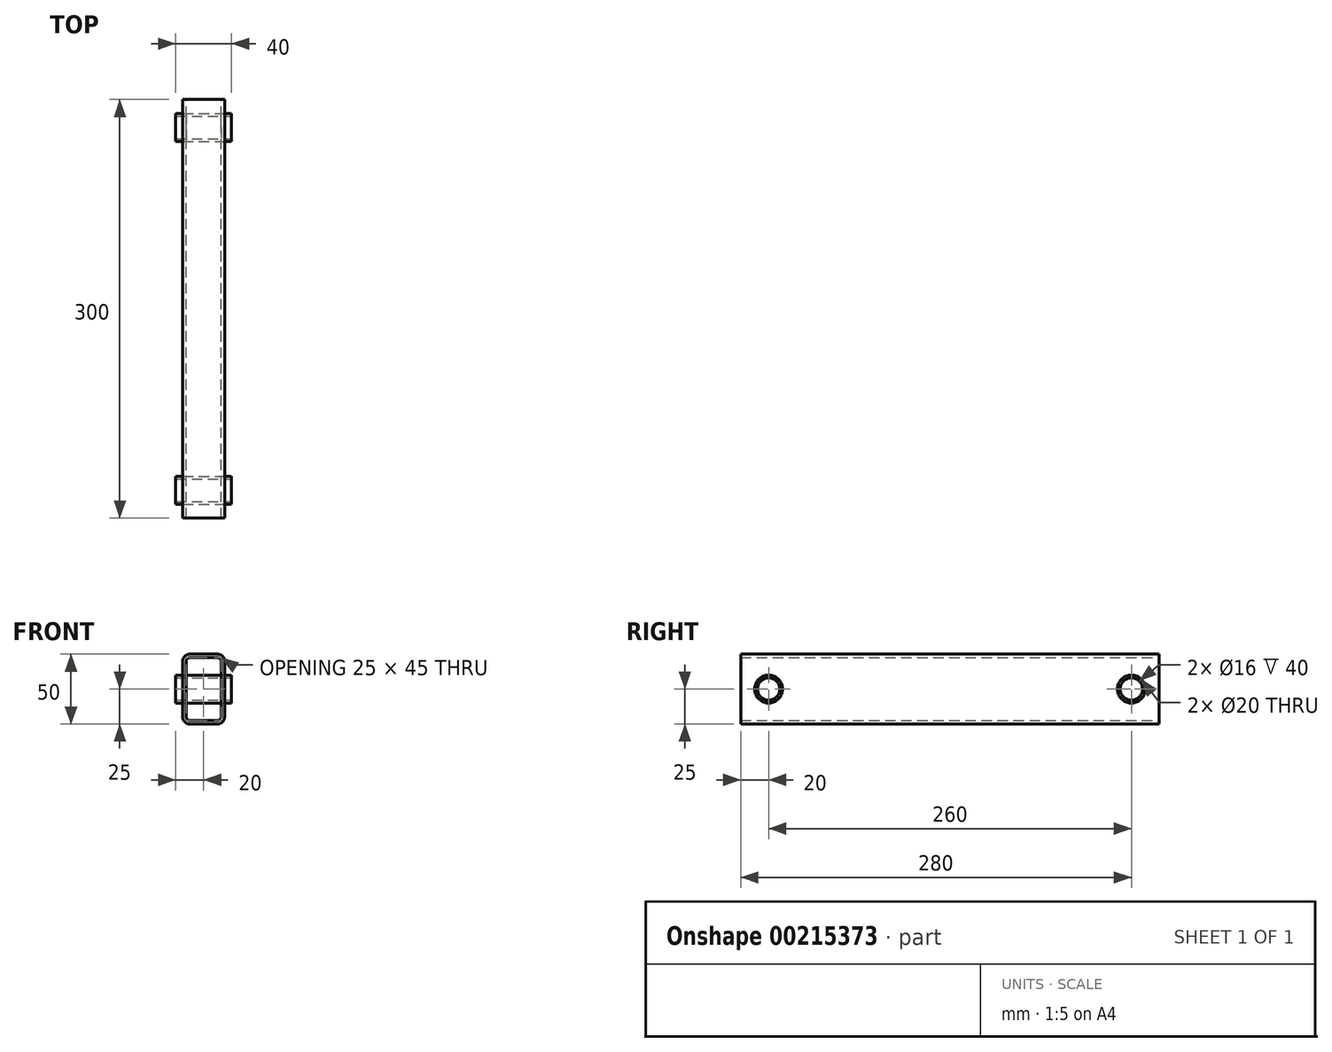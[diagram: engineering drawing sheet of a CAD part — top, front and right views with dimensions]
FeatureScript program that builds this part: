
annotation { "Feature Type Name" : "Feature", "Feature Type Description" : "" }
export const myFeature = defineFeature(function(context is Context, id is Id, definition is map)
    precondition{}
    {
        {
            var Q0;
            Q0=qCreatedBy(makeId("Front.planeOp"),FACE);
            var sketch = newSketch(context, id + "F0", { "sketchPlane" : qUnion([Q0])});
            skLineSegment(sketch, "E0.bottom", {"start": v(10, -25) * mm, "end": v(-10, -25) * mm});
            skLineSegment(sketch, "E0.top", {"start": v(10, 25) * mm, "end": v(-10, 25) * mm});
            skLineSegment(sketch, "E0.left", {"start": v(15, -20) * mm, "end": v(15, 20) * mm});
            skLineSegment(sketch, "E0.right", {"start": v(-15, -20) * mm, "end": v(-15, 20) * mm});
            skPoint(sketch, "E0.middle", {"position": v(0, 0) * mm});
            skPoint(sketch, "E1.visualSharp", {"position": v(-15, 25) * mm});
            skArc(sketch, "E1.filletArc", {"start": v(-10, 25) * mm, "mid": v(-13.54, 23.54) * mm, "end": v(-15, 20) * mm});
            skPoint(sketch, "E2.visualSharp", {"position": v(-15, -25) * mm});
            skArc(sketch, "E2.filletArc", {"start": v(-15, -20) * mm, "mid": v(-13.54, -23.54) * mm, "end": v(-10, -25) * mm});
            skPoint(sketch, "E3.visualSharp", {"position": v(15, -25) * mm});
            skArc(sketch, "E3.filletArc", {"start": v(10, -25) * mm, "mid": v(13.54, -23.54) * mm, "end": v(15, -20) * mm});
            skPoint(sketch, "E4.visualSharp", {"position": v(15, 25) * mm});
            skArc(sketch, "E4.filletArc", {"start": v(15, 20) * mm, "mid": v(13.54, 23.54) * mm, "end": v(10, 25) * mm});
            skSolve(sketch);
        }
        {
            var Q0;
            Q0 = qSketchRegion(id + "F0", true);
            var Q1;
            Q1=sQuery(id+"F0.wireOp",EDGE,"E0.top");
            var Q2;
            Q2=sQuery(id+"F0.wireOp",EDGE,"E4.filletArc");
            var Q3;
            Q3=sQuery(id+"F0.wireOp",EDGE,"E0.left");
            var Q4;
            Q4=sQuery(id+"F0.wireOp",EDGE,"E3.filletArc");
            var Q5;
            Q5=sQuery(id+"F0.wireOp",EDGE,"E0.bottom");
            var Q6;
            Q6=sQuery(id+"F0.wireOp",EDGE,"E2.filletArc");
            var Q7;
            Q7=sQuery(id+"F0.wireOp",EDGE,"E0.right");
            var Q8;
            Q8=sQuery(id+"F0.wireOp",EDGE,"E1.filletArc");
            extrude(context, id + "F1", {"entities" : qUnion([Q0]), "surfaceEntities" : qUnion([Q1, Q2, Q3, Q4, Q5, Q6, Q7, Q8]), "endBound" : BoundingType.SYMMETRIC, "depth" : 300 * mm});
        }
        {
            var Q0;
            Q0=makeQuery(id+"F1.opExtrude","CAP_FACE",FACE,{"disambiguationData":[OSD([sQuery(id+"F0.wireOp",EDGE,"E0.bottom"),sQuery(id+"F0.wireOp",EDGE,"E0.top"),sQuery(id+"F0.wireOp",EDGE,"E0.left"),sQuery(id+"F0.wireOp",EDGE,"E0.right"),sQuery(id+"F0.wireOp",EDGE,"E1.filletArc"),sQuery(id+"F0.wireOp",EDGE,"E2.filletArc"),sQuery(id+"F0.wireOp",EDGE,"E3.filletArc"),sQuery(id+"F0.wireOp",EDGE,"E4.filletArc")])],"isStart":false});
            var Q1;
            Q1=makeQuery(id+"F1.opExtrude","CAP_FACE",FACE,{"disambiguationData":[OSD([sQuery(id+"F0.wireOp",EDGE,"E0.bottom"),sQuery(id+"F0.wireOp",EDGE,"E0.top"),sQuery(id+"F0.wireOp",EDGE,"E0.left"),sQuery(id+"F0.wireOp",EDGE,"E0.right"),sQuery(id+"F0.wireOp",EDGE,"E1.filletArc"),sQuery(id+"F0.wireOp",EDGE,"E2.filletArc"),sQuery(id+"F0.wireOp",EDGE,"E3.filletArc"),sQuery(id+"F0.wireOp",EDGE,"E4.filletArc")])],"isStart":true});
            shell(context, id + "F2", {"entities" : qUnion([Q0, Q1]), "thickness" : 2.5 * mm});
        }
        {
            var Q0;
            Q0=makeQuery(id+"F1.opExtrude","SWEPT_FACE",FACE,{"disambiguationData":[OSD([sQuery(id+"F0.wireOp",EDGE,"E0.left")])]});
            var sketch = newSketch(context, id + "F3", { "sketchPlane" : qUnion([Q0])});
            skCircle(sketch, "E5", {"center": v(130, 0) * mm, "radius": 10 * mm});
            skSolve(sketch);
        }
        {
            var Q0;
            Q0 = qSketchRegion(id + "F3", true);
            extrude(context, id + "F4", {"entities" : qUnion([Q0]), "operationType" : NewBodyOperationType.REMOVE, "endBound" : BoundingType.THROUGH_ALL, "oppositeDirection" : true, "depth" : 25 * mm});
        }
        {
            var Q0;
            Q0=makeQuery(id+"F1.opExtrude","SWEPT_FACE",FACE,{"disambiguationData":[OSD([sQuery(id+"F0.wireOp",EDGE,"E0.left")])]});
            cPlane(context, id + "F5", {"entities" : qUnion([Q0]), "cplaneType" : CPlaneType.OFFSET, "offset" : 5 * mm, "width" : 150 * mm, "height" : 150 * mm});
        }
        {
            var Q0;
            Q0=makeQuery(id+"F1.opExtrude","SWEPT_FACE",FACE,{"disambiguationData":[OSD([sQuery(id+"F0.wireOp",EDGE,"E0.right")])]});
            cPlane(context, id + "F6", {"entities" : qUnion([Q0]), "cplaneType" : CPlaneType.OFFSET, "offset" : 5 * mm, "width" : 150 * mm, "height" : 150 * mm});
        }
        {
            var Q0;
            Q0=qCreatedBy(id+"F5.planeOp",FACE);
            var sketch = newSketch(context, id + "F7", { "sketchPlane" : qUnion([Q0])});
            skCircle(sketch, "E6.0", {"center": v(130, 0) * mm, "radius": 10 * mm});
            skCircle(sketch, "E7", {"center": v(130, 0) * mm, "radius": 8 * mm});
            skSolve(sketch);
        }
        {
            var Q0;
            Q0 = qSketchRegion(id + "F7", true);
            var Q1;
            Q1=qCreatedBy(id+"F6.planeOp",FACE);
            extrude(context, id + "F8", {"entities" : qUnion([Q0]), "endBound" : BoundingType.UP_TO_SURFACE, "oppositeDirection" : true, "endBoundEntityFace" : qUnion([Q1]), "depth" : 25 * mm});
        }
        {
            var Q0;
            Q0=makeQuery(id+"F8.opExtrude","SWEPT_BODY",BODY,{"disambiguationData":[OSD([sQuery(id+"F7.wireOp",EDGE,"E6.0"),sQuery(id+"F7.wireOp",EDGE,"E7")])]});
            var Q1;
            Q1=qCreatedBy(makeId("Front.planeOp"),FACE);
            mirror(context, id + "F9", {"entities" : qUnion([Q0]), "mirrorPlane" : qUnion([Q1])});
        }
    });
